# Revit family: Solarstone_Solar_Full_Roof_Landscape_Filler_module
name_source: partatom
category: Curtain Panels
units: mm (PartAtom-declared; Revit-internal decimal feet)

## family parameters
Always vertical = No
Cut with Voids When Loaded = No
OmniClass Number = 23.25.20.14.11.11.17
OmniClass Title = Infill Panels
Shared = No

## types (3) — shared parameters
Analytic Construction = <None>
Brand URL = https://solarstone.com
Date of Publishing = 12.03.2026
Define Thermal Properties by = Schematic Type
Depth = 35 mm
Design Country = Estonia
Edition Number = 1
Manufacturer Country = Estonia
Manufacturer Name = Solarstone
Minimum Lenght = Filler Panels must be at least 300 mm in lenght for application
Overlap = 55 mm  [stored 0.180446 ft]
Panel_Category = Filler
Product Family = Energy
Product Group = Bulding Integrated PV-panels
Slope Requirement = Below 18 degrees of roof slope the system requires additional components to be installed below the sub structure
Width = 1791 mm

## per-type parameters (varying)
| type | Default Height |
| KIT-A | 1195 mm  [stored 3.9206 ft] |
| KIT-B | 1245 mm |
| KIT-C | 1295 mm |

note: [stored X ft] marks values corroborated as IEEE doubles in the binary element streams (Revit-internal decimal feet)

## geometry (parser evidence)
native form markers: Sweep x2
no freeform markers — native parametric forms only
